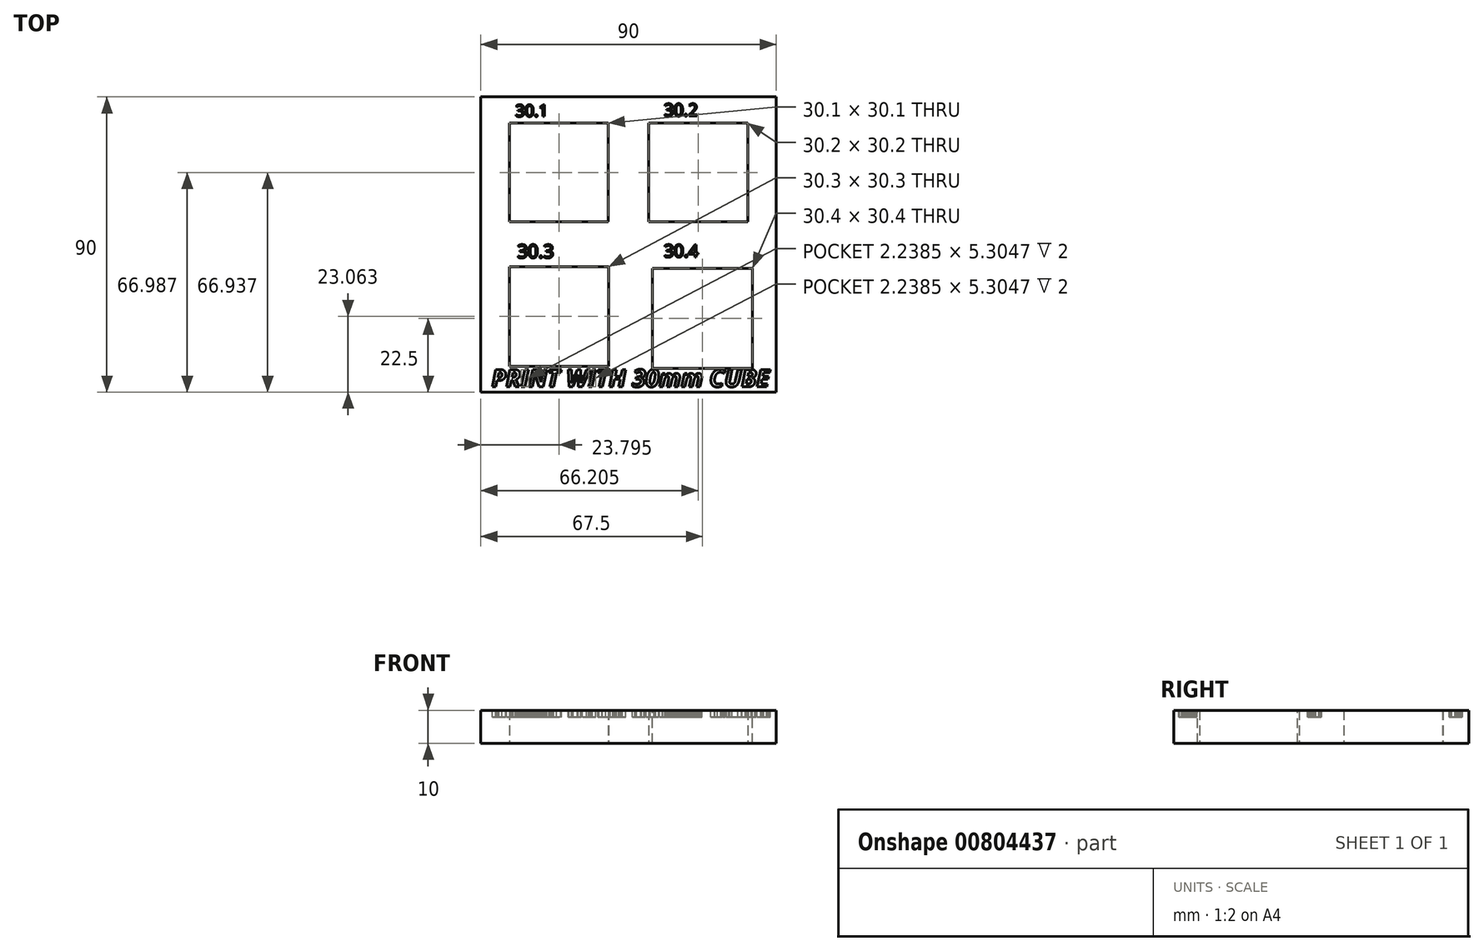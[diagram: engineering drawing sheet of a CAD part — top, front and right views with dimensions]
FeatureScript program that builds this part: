
annotation { "Feature Type Name" : "Feature", "Feature Type Description" : "" }
export const myFeature = defineFeature(function(context is Context, id is Id, definition is map)
    precondition{}
    {
        {
            var Q0;
            Q0=qCreatedBy(makeId("Top.planeOp"),FACE);
            var sketch = newSketch(context, id + "F0", { "sketchPlane" : qUnion([Q0])});
            skLineSegment(sketch, "E0.bottom", {"start": v(45, -45) * mm, "end": v(-45, -45) * mm});
            skLineSegment(sketch, "E0.top", {"start": v(45, 45) * mm, "end": v(-45, 45) * mm});
            skLineSegment(sketch, "E0.left", {"start": v(45, -45) * mm, "end": v(45, 45) * mm});
            skLineSegment(sketch, "E0.right", {"start": v(-45, -45) * mm, "end": v(-45, 45) * mm});
            skPoint(sketch, "E0.middle", {"position": v(0, 0) * mm});
            skPoint(sketch, "E1", {"position": v(-21.2, 21.94) * mm});
            skPoint(sketch, "E2", {"position": v(-21.2, -21.94) * mm});
            skPoint(sketch, "E3.start.orphan", {"position": v(-22.5, 0) * mm});
            skPoint(sketch, "E4.MirrorCS.start.orphan", {"position": v(22.5, 0) * mm});
            skLineSegment(sketch, "E5.bottom", {"start": v(-6.15, 6.89) * mm, "end": v(-36.25, 6.89) * mm});
            skLineSegment(sketch, "E5.top", {"start": v(-6.15, 36.99) * mm, "end": v(-36.25, 36.99) * mm});
            skLineSegment(sketch, "E5.left", {"start": v(-6.15, 6.89) * mm, "end": v(-6.15, 36.99) * mm});
            skLineSegment(sketch, "E5.right", {"start": v(-36.25, 6.89) * mm, "end": v(-36.25, 36.99) * mm});
            skLineSegment(sketch, "E6.bottom", {"start": v(36.3, 6.89) * mm, "end": v(6.1, 6.89) * mm});
            skLineSegment(sketch, "E6.top", {"start": v(36.3, 37.09) * mm, "end": v(6.1, 37.09) * mm});
            skLineSegment(sketch, "E6.left", {"start": v(36.3, 6.89) * mm, "end": v(36.3, 37.09) * mm});
            skLineSegment(sketch, "E6.right", {"start": v(6.1, 6.89) * mm, "end": v(6.1, 37.09) * mm});
            skLineSegment(sketch, "E7.bottom", {"start": v(-6.05, -37.09) * mm, "end": v(-36.35, -37.09) * mm});
            skLineSegment(sketch, "E7.top", {"start": v(-6.05, -6.79) * mm, "end": v(-36.35, -6.79) * mm});
            skLineSegment(sketch, "E7.left", {"start": v(-6.05, -37.09) * mm, "end": v(-6.05, -6.79) * mm});
            skLineSegment(sketch, "E7.right", {"start": v(-36.35, -37.09) * mm, "end": v(-36.35, -6.79) * mm});
            skSolve(sketch);
        }
        {
            var Q0;
            Q0 = qSketchRegion(id + "F0", true);
            extrude(context, id + "F1", {"entities" : qUnion([Q0]), "depth" : 10 * mm, "offsetDistance" : 25 * mm});
        }
        {
            var Q0;
            Q0=makeQuery(id+"F1.opExtrude","CAP_FACE",FACE,{"disambiguationData":[OSD([sQuery(id+"F0.wireOp",EDGE,"E0.bottom"),sQuery(id+"F0.wireOp",EDGE,"E0.top"),sQuery(id+"F0.wireOp",EDGE,"E0.left"),sQuery(id+"F0.wireOp",EDGE,"E0.right"),sQuery(id+"F0.wireOp",EDGE,"E5.bottom"),sQuery(id+"F0.wireOp",EDGE,"E5.top"),sQuery(id+"F0.wireOp",EDGE,"E5.left"),sQuery(id+"F0.wireOp",EDGE,"E5.right"),sQuery(id+"F0.wireOp",EDGE,"E6.bottom"),sQuery(id+"F0.wireOp",EDGE,"E6.top"),sQuery(id+"F0.wireOp",EDGE,"E6.left"),sQuery(id+"F0.wireOp",EDGE,"E6.right"),sQuery(id+"F0.wireOp",EDGE,"E7.bottom"),sQuery(id+"F0.wireOp",EDGE,"E7.top"),sQuery(id+"F0.wireOp",EDGE,"E7.left"),sQuery(id+"F0.wireOp",EDGE,"E7.right")])],"isStart":false});
            var sketch = newSketch(context, id + "F2", { "sketchPlane" : qUnion([Q0])});
            skText(sketch, "E8", { "text": "30.1\n", "fontName": "OpenSans-Regular.ttf"});
            skText(sketch, "E9", { "text": "30.2\n", "fontName": "OpenSans-Regular.ttf"});
            skText(sketch, "E10", { "text": "30.3\n", "fontName": "OpenSans-Regular.ttf"});
            skPoint(sketch, "E10.secondSnap0", {"position": v(-21.2, -6.79) * mm});
            skLineSegment(sketch, "E11", {"start": v(0, 0) * mm, "end": v(22.5, 0) * mm});
            skLineSegment(sketch, "E12", {"start": v(22.5, 0) * mm, "end": v(22.5, -22.5) * mm});
            skLineSegment(sketch, "E13.bottom", {"start": v(37.7, -37.7) * mm, "end": v(7.3, -37.7) * mm});
            skLineSegment(sketch, "E13.top", {"start": v(37.7, -7.3) * mm, "end": v(7.3, -7.3) * mm});
            skLineSegment(sketch, "E13.left", {"start": v(37.7, -37.7) * mm, "end": v(37.7, -7.3) * mm});
            skLineSegment(sketch, "E13.right", {"start": v(7.3, -37.7) * mm, "end": v(7.3, -7.3) * mm});
            skPoint(sketch, "E13.middle", {"position": v(22.5, -22.5) * mm});
            skText(sketch, "E14", { "text": "30.4\n", "fontName": "OpenSans-Regular.ttf"});
            const initialGuessF2  = {"E8": [-0.03567, 0.03863, 1, 0, 0.00503], "E9": [0.0061, 0.03878, 1, 0, 0.00414], "E10": [-0.03183, -0.00512, 1, 0, 0.00385], "E14": [0.00198, -0.00575, 1, 0, 0.0037]};
            skSetInitialGuess(sketch, initialGuessF2);
            skSolve(sketch);
        }
        {
            var Q0;
            Q0=makeQuery(id+"F2.imprint","IMPRINT",FACE,{"disambiguationData":[TD([[makeQuery(id+"F2.imprint","IMPRINT",EDGE,{"derivedFrom":sQuery(id+"F2.wireOp",EDGE,"E13.bottom")}),-1.0]])]});
            extrude(context, id + "F3", {"entities" : qUnion([Q0]), "operationType" : NewBodyOperationType.REMOVE, "oppositeDirection" : true, "depth" : 25 * mm, "offsetDistance" : 25 * mm});
        }
        {
            var Q0;
            Q0=makeQuery(id+"F1.opExtrude","CAP_FACE",FACE,{"disambiguationData":[OSD([sQuery(id+"F0.wireOp",EDGE,"E0.bottom"),sQuery(id+"F0.wireOp",EDGE,"E0.top"),sQuery(id+"F0.wireOp",EDGE,"E0.left"),sQuery(id+"F0.wireOp",EDGE,"E0.right"),sQuery(id+"F0.wireOp",EDGE,"E5.bottom"),sQuery(id+"F0.wireOp",EDGE,"E5.top"),sQuery(id+"F0.wireOp",EDGE,"E5.left"),sQuery(id+"F0.wireOp",EDGE,"E5.right"),sQuery(id+"F0.wireOp",EDGE,"E6.bottom"),sQuery(id+"F0.wireOp",EDGE,"E6.top"),sQuery(id+"F0.wireOp",EDGE,"E6.left"),sQuery(id+"F0.wireOp",EDGE,"E6.right"),sQuery(id+"F0.wireOp",EDGE,"E7.bottom"),sQuery(id+"F0.wireOp",EDGE,"E7.top"),sQuery(id+"F0.wireOp",EDGE,"E7.left"),sQuery(id+"F0.wireOp",EDGE,"E7.right")])],"isStart":false});
            var sketch = newSketch(context, id + "F4", { "sketchPlane" : qUnion([Q0])});
            skText(sketch, "E15", { "text": "30.1\n", "fontName": "OpenSans-Regular.ttf"});
            skText(sketch, "E16", { "text": "30.2\n", "fontName": "OpenSans-Regular.ttf"});
            skPoint(sketch, "E16.secondSnap0", {"position": v(21.2, 37.09) * mm});
            skText(sketch, "E17", { "text": "30.3\n", "fontName": "OpenSans-Regular.ttf"});
            skText(sketch, "E18", { "text": "30.4\n", "fontName": "OpenSans-Regular.ttf"});
            const initialGuessF4  = {"E15": [-0.03447, 0.03902, 1, 0, 0.0036], "E16": [0.01078, 0.03917, 1, 0, 0.00377], "E17": [-0.03394, -0.00407, 1, 0, 0.00407], "E18": [0.01077, -0.00382, 1, 0, 0.00382]};
            skSetInitialGuess(sketch, initialGuessF4);
            skSolve(sketch);
        }
        {
            var Q0;
            Q0 = qSketchRegion(id + "F4", true);
            extrude(context, id + "F5", {"entities" : qUnion([Q0]), "operationType" : NewBodyOperationType.REMOVE, "oppositeDirection" : true, "depth" : 2 * mm, "offsetDistance" : 25 * mm});
        }
        {
            var Q0;
            {var subQ0=sQuery(id+"F0.wireOp",EDGE,"E6.bottom");var subQ1=sQuery(id+"F0.wireOp",EDGE,"E6.top");var subQ2=sQuery(id+"F0.wireOp",EDGE,"E0.bottom");var subQ3=sQuery(id+"F0.wireOp",EDGE,"E0.right");var subQ4=sQuery(id+"F0.wireOp",EDGE,"E0.top");var subQ5=sQuery(id+"F0.wireOp",EDGE,"E0.left");var subQ6=sQuery(id+"F0.wireOp",EDGE,"E6.left");var subQ7=sQuery(id+"F0.wireOp",EDGE,"E6.right");var subQ8=sQuery(id+"F0.wireOp",EDGE,"E5.bottom");var subQ9=sQuery(id+"F0.wireOp",EDGE,"E7.bottom");var subQ10=sQuery(id+"F0.wireOp",EDGE,"E5.top");var subQ11=sQuery(id+"F0.wireOp",EDGE,"E7.top");var subQ12=sQuery(id+"F0.wireOp",EDGE,"E5.left");var subQ13=sQuery(id+"F0.wireOp",EDGE,"E7.left");var subQ14=sQuery(id+"F0.wireOp",EDGE,"E5.right");var subQ15=sQuery(id+"F0.wireOp",EDGE,"E7.right");Q0=makeQuery(id+"F5.boolean.opBoolean","SPLIT",FACE,{"disambiguationData":[TD([makeQuery(id+"F1.opExtrude","SWEPT_FACE",FACE,{"disambiguationData":[OSD([subQ2])]})])],"derivedFrom":makeQuery(id+"F1.opExtrude","CAP_FACE",FACE,{"disambiguationData":[OSD([subQ2,subQ4,subQ5,subQ3,subQ8,subQ10,subQ12,subQ14,subQ0,subQ1,subQ6,subQ7,subQ9,subQ11,subQ13,subQ15])],"isStart":false})});}
            var sketch = newSketch(context, id + "F6", { "sketchPlane" : qUnion([Q0])});
            skText(sketch, "E19", { "text": "PRINT WITH 30mm CUBE", "fontName": "OpenSans-BoldItalic.ttf"});
            const initialGuessF6  = {"E19": [-0.04174, -0.04339, 1, 0, 0.00535]};
            skSetInitialGuess(sketch, initialGuessF6);
            skSolve(sketch);
        }
        {
            var Q0;
            Q0 = qSketchRegion(id + "F6", true);
            extrude(context, id + "F7", {"entities" : qUnion([Q0]), "operationType" : NewBodyOperationType.REMOVE, "oppositeDirection" : true, "depth" : 2 * mm, "offsetDistance" : 25 * mm});
        }
    });
